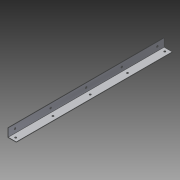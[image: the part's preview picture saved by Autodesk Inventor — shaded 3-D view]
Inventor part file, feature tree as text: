
AUTODESK INVENTOR PART (.ipt)
format: ipt  version: 2014 SP1 (Build 180222100, 222)  size: 106,496 bytes
history: native  units: in
note: dims shown in document units (in); Inventor stores cm internally (conversion verified against a paired STEP export)
features: extrude x3, sketch x3
ambient origin geometry x8: Origin, YZ Plane, XZ Plane, XY Plane, X Axis, Y Axis, Z Axis, Center Point
bodies: Solid1 (feature_tree)
feature tree (6):
  extrude  "Extrusion1"  Depth=0.0312in
  sketch  "Sketch2"  dims[d2=11.5in d3=0.0in d4=0.25in]
  sketch  "Sketch3"  dims[d5=0.125in d6=11.5in d7=1.9685in d9=2.75in d10=0.3937in d12=1.0in d14=0.125in d15=0.5in d16=11.5in d17=1.9685in d19=2.625in d20=0.3937in d22=1.0in d24=1.0in d25=0.0in d26=1.0in d27=0.0in]
  extrude  "Extrusion2"  Depth=11.5in
  extrude  "Extrusion3"  Depth=11.5in
  sketch  "Sketch1"  dims[d0=0.625in d1=0.0312in]
